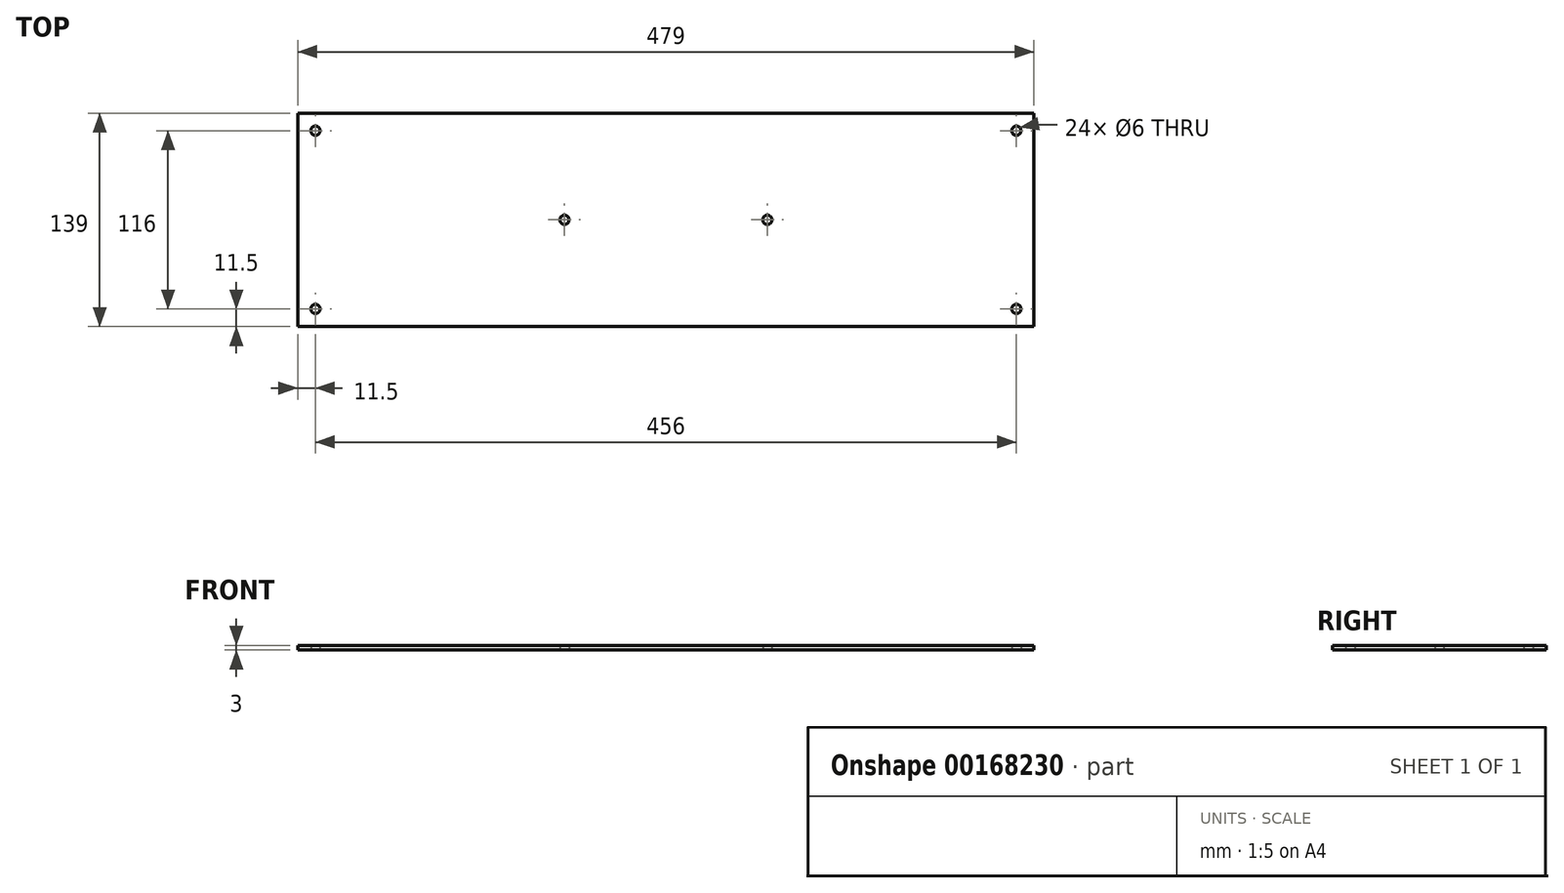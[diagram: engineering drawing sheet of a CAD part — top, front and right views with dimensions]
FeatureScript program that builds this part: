
annotation { "Feature Type Name" : "Feature", "Feature Type Description" : "" }
export const myFeature = defineFeature(function(context is Context, id is Id, definition is map)
    precondition{}
    {
        {
            var Q0;
            Q0=qCreatedBy(makeId("Top.planeOp"),FACE);
            var sketch = newSketch(context, id + "F0", { "sketchPlane" : qUnion([Q0])});
            skLineSegment(sketch, "E0.bottom", {"start": v(239.5, -69.5) * mm, "end": v(-239.5, -69.5) * mm});
            skLineSegment(sketch, "E0.top", {"start": v(239.5, 69.5) * mm, "end": v(-239.5, 69.5) * mm});
            skLineSegment(sketch, "E0.left", {"start": v(239.5, -69.5) * mm, "end": v(239.5, 69.5) * mm});
            skLineSegment(sketch, "E0.right", {"start": v(-239.5, -69.5) * mm, "end": v(-239.5, 69.5) * mm});
            skPoint(sketch, "E0.middle", {"position": v(0, 0) * mm});
            skLineSegment(sketch, "E1.0", {"start": v(228, 58) * mm, "end": v(-228, 58) * mm, "construction": true});
            skLineSegment(sketch, "E1.1", {"start": v(228, -58) * mm, "end": v(228, 58) * mm, "construction": true});
            skLineSegment(sketch, "E1.2", {"start": v(228, -58) * mm, "end": v(-228, -58) * mm, "construction": true});
            skLineSegment(sketch, "E1.3", {"start": v(-228, -58) * mm, "end": v(-228, 58) * mm, "construction": true});
            skCircle(sketch, "E2", {"center": v(-228, 58) * mm, "radius": 3 * mm});
            skCircle(sketch, "E3", {"center": v(-228, -58) * mm, "radius": 3 * mm});
            skCircle(sketch, "E4", {"center": v(228, 58) * mm, "radius": 3 * mm});
            skCircle(sketch, "E5", {"center": v(228, -58) * mm, "radius": 3 * mm});
            skLineSegment(sketch, "E6", {"start": v(-66, 0) * mm, "end": v(66, 0) * mm, "construction": true});
            skLineSegment(sketch, "E7", {"start": v(0, 69.5) * mm, "end": v(0, -69.5) * mm, "construction": true});
            skCircle(sketch, "E8", {"center": v(-66, 0) * mm, "radius": 3 * mm});
            skCircle(sketch, "E9", {"center": v(66, 0) * mm, "radius": 3 * mm});
            skSolve(sketch);
        }
        {
            var Q0;
            Q0 = qSketchRegion(id + "F0", true);
            extrude(context, id + "F1", {"entities" : qUnion([Q0]), "depth" : 3 * mm});
        }
    });
